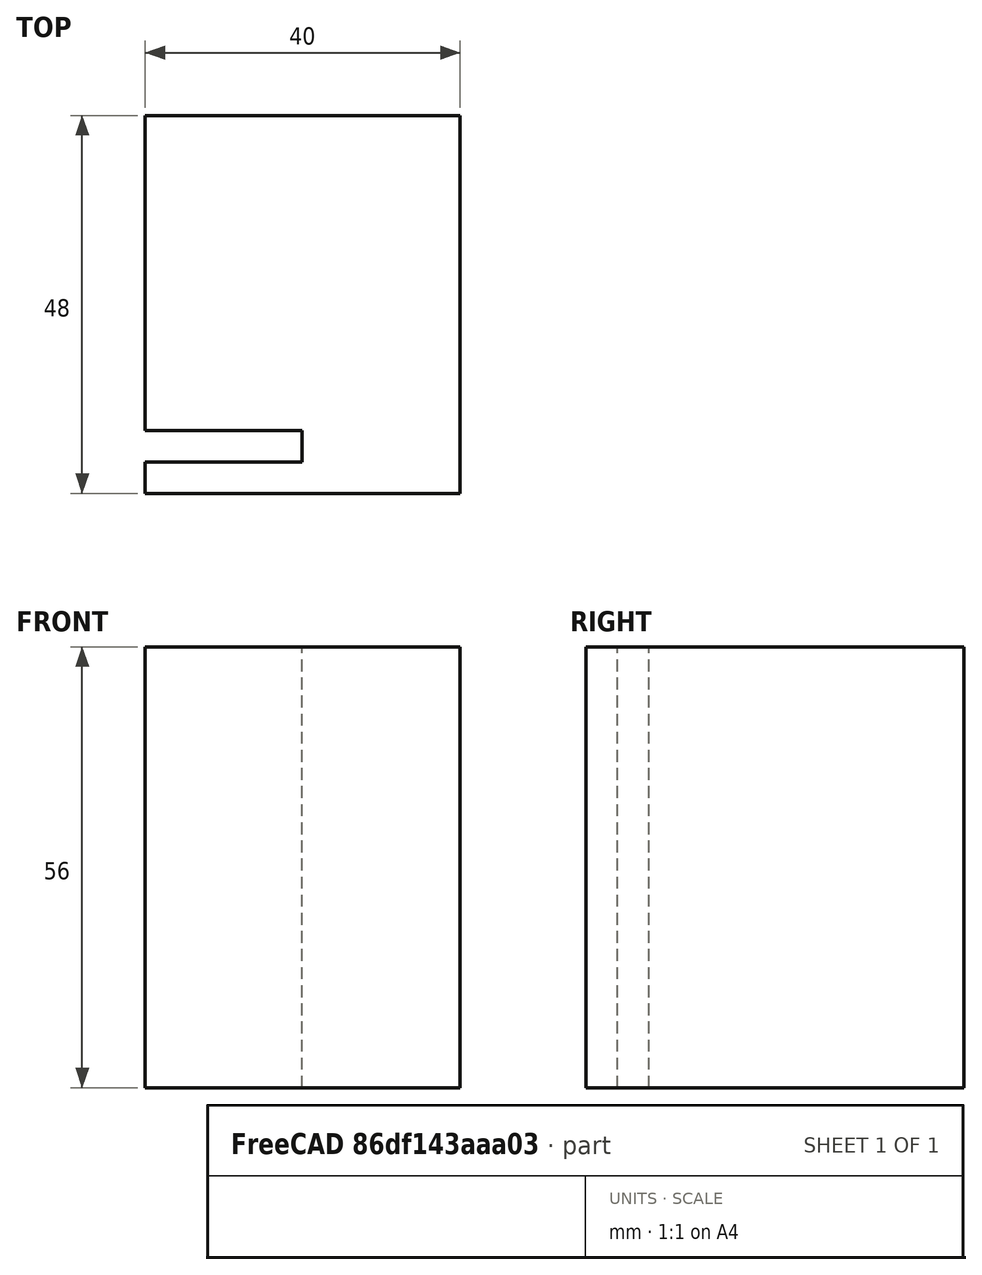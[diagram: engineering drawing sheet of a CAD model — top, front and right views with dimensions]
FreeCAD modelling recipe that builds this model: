
FCSTD DOCUMENT  (FreeCAD 0.18.4R)
Label: sensor-body
License: All rights reserved
LicenseURL: http://en.wikipedia.org/wiki/All_rights_reserved
objects: Sketcher::SketchObject×1, PartDesign::Pad×1, PartDesign::Body×1
note: 4 computed .brp shape members not serialized (recipe doc carries the construction recipe); baked Part::Feature solids carry a one-line shape summary decoded from their .brp

FEATURE [Sketcher::SketchObject] Sketch
  MapMode = 5
  Support = -> [XY_Plane]
  sketch-geometry (8):
    g0: LineSegment StartX=0 StartY=0 StartZ=0 EndX=0 EndY=40 EndZ=0
    g1: LineSegment StartX=0 StartY=40 StartZ=0 EndX=40 EndY=40 EndZ=0
    g2: LineSegment StartX=40 StartY=40 StartZ=0 EndX=40 EndY=-8 EndZ=0
    g3: LineSegment StartX=40 StartY=-8 StartZ=0 EndX=0 EndY=-8 EndZ=0
    g4: LineSegment StartX=0 StartY=-8 StartZ=0 EndX=0 EndY=-4 EndZ=0
    g5: LineSegment StartX=0 StartY=-4 StartZ=0 EndX=20 EndY=-4 EndZ=0
    g6: LineSegment StartX=20 StartY=-4 StartZ=0 EndX=20 EndY=0 EndZ=0
    g7: LineSegment StartX=20 StartY=0 StartZ=0 EndX=0 EndY=0 EndZ=0
  constraints (21):
    c: Coincident(g-1,g0)
    c: Vertical(g0)
    c: Coincident(g0,g1)
    c: Horizontal(g1)
    c: Coincident(g1,g2)
    c: Vertical(g2)
    c: Coincident(g2,g3)
    c: Horizontal(g3)
    c: Coincident(g3,g4)
    c: Vertical(g4)
    c: Coincident(g4,g5)
    c: Horizontal(g5)
    c: Coincident(g5,g6)
    c: Vertical(g6)
    c: Coincident(g6,g7)
    c: Coincident(g7,g0)
    c: Horizontal(g7)
    c: DistanceX(g1,g1) = 40
    c: DistanceX(g7,g7) = 20
    c: Equal(g5,g7)
    c: Equal(g3,g1)
FEATURE [PartDesign::Pad] Pad
  Length = 56
  Length2 = 100
  Midplane = true
  Profile = -> Sketch
  Type = 0
FEATURE [PartDesign::Body] Body
  Group = -> [Sketch,Pad]
  Origin = -> Origin
  Tip = -> Pad
